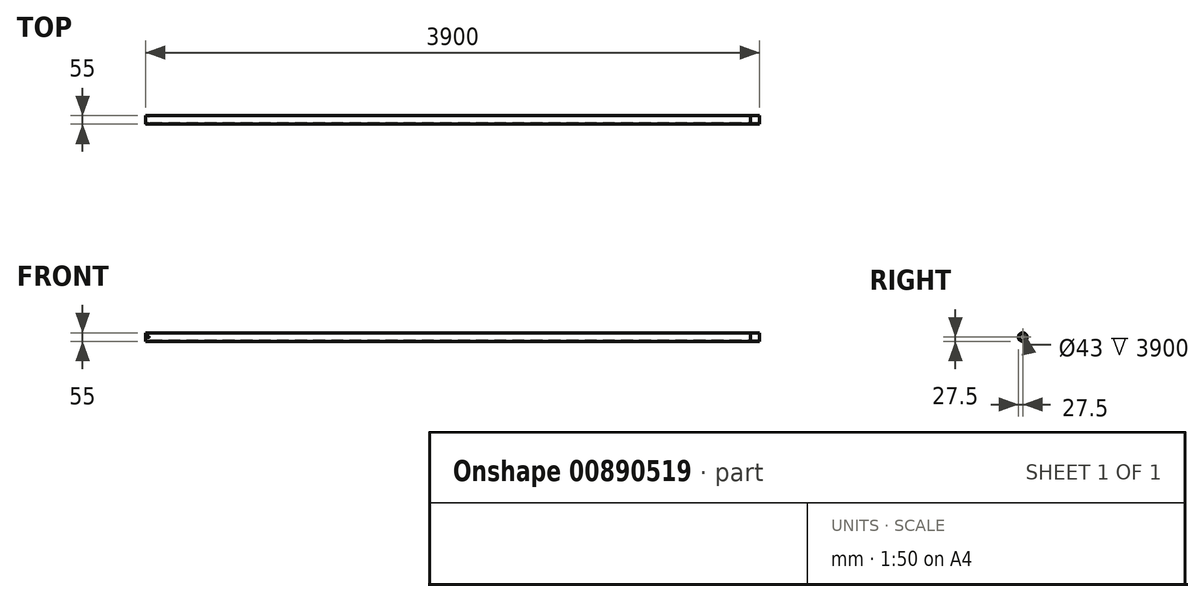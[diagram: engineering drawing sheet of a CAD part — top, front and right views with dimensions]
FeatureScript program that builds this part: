
annotation { "Feature Type Name" : "Feature", "Feature Type Description" : "" }
export const myFeature = defineFeature(function(context is Context, id is Id, definition is map)
    precondition{}
    {
        {
            var Q0;
            Q0=qCreatedBy(makeId("Right.planeOp"),FACE);
            var sketch = newSketch(context, id + "F0", { "sketchPlane" : qUnion([Q0])});
            skCircle(sketch, "E0", {"center": v(0, 0) * mm, "radius": 21.5 * mm});
            skCircle(sketch, "E1", {"center": v(0, 0) * mm, "radius": 27.5 * mm});
            skSolve(sketch);
        }
        {
            var Q0;
            Q0 = qSketchRegion(id + "F0", true);
            extrude(context, id + "F1", {"entities" : qUnion([Q0]), "endBound" : BoundingType.SYMMETRIC, "depth" : 3900 * mm, "offsetDistance" : 25 * mm});
        }
        {
            var Q0;
            Q0=makeQuery(id+"F1.opExtrude","CAP_FACE",FACE,{"disambiguationData":[OSD([sQuery(id+"F0.wireOp",EDGE,"E0"),sQuery(id+"F0.wireOp",EDGE,"E1")])],"isStart":false});
            var sketch = newSketch(context, id + "F2", { "sketchPlane" : qUnion([Q0])});
            skCircle(sketch, "E2", {"center": v(0, 0) * mm, "radius": 28 * mm});
            skCircle(sketch, "E3", {"center": v(0, 0) * mm, "radius": 27 * mm});
            skSolve(sketch);
        }
        {
            var Q0;
            Q0 = qSketchRegion(id + "F2", true);
            extrude(context, id + "F3", {"entities" : qUnion([Q0]), "operationType" : NewBodyOperationType.REMOVE, "oppositeDirection" : true, "depth" : 58 * mm, "offsetDistance" : 25 * mm});
        }
        {
            var Q0;
            Q0=qCreatedBy(makeId("Front.planeOp"),FACE);
            var sketch = newSketch(context, id + "F4", { "sketchPlane" : qUnion([Q0])});
            skArc(sketch, "E4", {"start": v(-1940.5, 3.5) * mm, "mid": v(-1944, 0) * mm, "end": v(-1940.5, -3.5) * mm});
            skLineSegment(sketch, "E5", {"start": v(-1940.5, -3.5) * mm, "end": v(-1931, -3.5) * mm});
            skLineSegment(sketch, "E6", {"start": v(-1931, 3.5) * mm, "end": v(-1940.5, 3.5) * mm});
            skArc(sketch, "E7", {"start": v(-1931, -3.5) * mm, "mid": v(-1927.5, 0) * mm, "end": v(-1931, 3.5) * mm});
            skSolve(sketch);
        }
        {
            var Q0;
            Q0 = qSketchRegion(id + "F4", true);
            extrude(context, id + "F5", {"entities" : qUnion([Q0]), "operationType" : NewBodyOperationType.REMOVE, "endBound" : BoundingType.SYMMETRIC, "oppositeDirection" : true, "depth" : 55 * mm, "offsetDistance" : 25 * mm});
        }
    });
